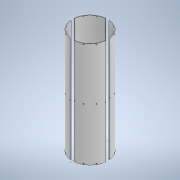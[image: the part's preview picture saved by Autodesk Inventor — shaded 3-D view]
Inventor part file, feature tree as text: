
AUTODESK INVENTOR PART (.ipt)
format: ipt  version: 2021 (Build 250183000, 183)  size: 347,648 bytes
history: native  units: in
note: dims shown in document units (in); Inventor stores cm internally (conversion verified against a paired STEP export)
features: other x24, pattern_circular x6, hole x6, sketch x5, plane x3, extrude x2
ambient origin geometry x8: Origin, YZ Plane, XZ Plane, XY Plane, X Axis, Y Axis, Z Axis, Center Point
bodies: Solid1 (feature_tree)
feature tree (46):
  extrude  "Extrusion1"  TaperAngle=0.0deg  [1 undecoded]
  plane  "Work Plane1"
  extrude  "Extrusion2"  Depth=0.3937in TaperAngle=0.0deg
  pattern_circular  "Circular Pattern1"  Count=4 Angle=360.0deg
  other  "Work Axis1"
  other  "Work Axis2"
  other  "Work Axis3"
  other  "Work Axis4"
  other  "Work Point1"
  other  "Work Point2"
  other  "Work Point3"
  other  "Central Plane"
  other  "Work Point4"
  other  "Work Axis6"
  other  "Work Axis7"
  other  "Offset Plane A"
  other  "Work Point5"
  other  "Work Point6"
  other  "Work Axis8"
  other  "Work Axis9"
  other  "Work Point7"
  other  "Work Point8"
  plane  "Work Plane5"
  plane  "Work Plane6"
  hole  "Hole1"  [1 undecoded]
  hole  "Hole2"  [1 undecoded]
  pattern_circular  "Circular Pattern3"  Count=4 Angle=360.0deg
  sketch  "Sketch5"  dims[d13=0.0484in d14=-11.811in]
  other  "Work Axis10"
  other  "plane for insert hole 1"
  sketch  "Sketch7"  dims[d15=0.0484in d16=0.1574in]
  other  "plane for insert hole 2"
  sketch  "Sketch8"  dims[d17=-0.1574in d48=1.0in d49=1.0in d29=0.096in d30=0.75in d31=0.185in d32=0.25in d33=0.5635in d34=1.0in d35=0.0in d52=1.0in d53=1.0in d38=0.096in d39=0.75in d40=0.185in d41=0.25in d42=0.5635in d43=1.0in d44=0.8108in d45=1.5748in d46=360.0deg d88=30.0deg d89=30.0deg d90=0.0in d91=0.0in d92=0.0in d93=11.811in d94=0.0in d95=11.811in d96=0.129in d97=0.224in d98=0.225in d99=0.25in d100=0.5635in d101=0.349in d102=0.8108in d103=0.129in d104=0.224in d105=0.225in d106=0.25in d107=0.5635in d108=0.349in d109=0.8108in d110=1.5748in d111=360.0deg d116=1.5748in d117=360.0deg d119=0.0in d120=0.0in d121=0.0in d122=0.1969in d123=0.1969in d124=0.0in d125=0.0in d126=0.1969in d127=0.1969in d128=0.129in d129=0.75in d130=0.225in d131=0.25in d132=0.5635in d133=0.349in d134=0.8108in d135=0.129in d136=0.75in d137=0.225in d138=0.25in d139=0.5635in d140=0.349in d141=0.8108in d142=1.5748in d143=360.0deg d145=1.5748in d146=360.0deg d54=1.0in d55=1.0in d56=1.0in d57=0.15in d58=0.25in d59=0.375in d60=0.5635in d61=0.75in d62=0.8108in d63=0.0625in d64=0.75in d65=0.375in]
  hole  "insert hole 2"  [1 undecoded]
  hole  "insert hole 1"  [1 undecoded]
  pattern_circular  "Circular Pattern7"  [2 undecoded]
  pattern_circular  "Circular Pattern9"  [2 undecoded]
  other  "Work Axis14"
  hole  "Hole8"  [1 undecoded]
  hole  "Hole9"  [1 undecoded]
  pattern_circular  "Circular Pattern10"  [2 undecoded]
  pattern_circular  "Circular Pattern11"  Count=30  [1 undecoded]
  sketch  "Sketch1"  dims[d3=0.0in d5=0.0in]
  sketch  "Sketch2"  dims[d7=0.3937in d8=0.5in d9=0.0in d10=1.5748in d11=360.0deg]
  other  "Work Axis5"
  other  "Offset Plane B"
note: 14 required parameter values undecoded (feature->parameter linkage not recoverable at this tier; creation-order binding heuristic only, values carry confidence <= 0.55)
